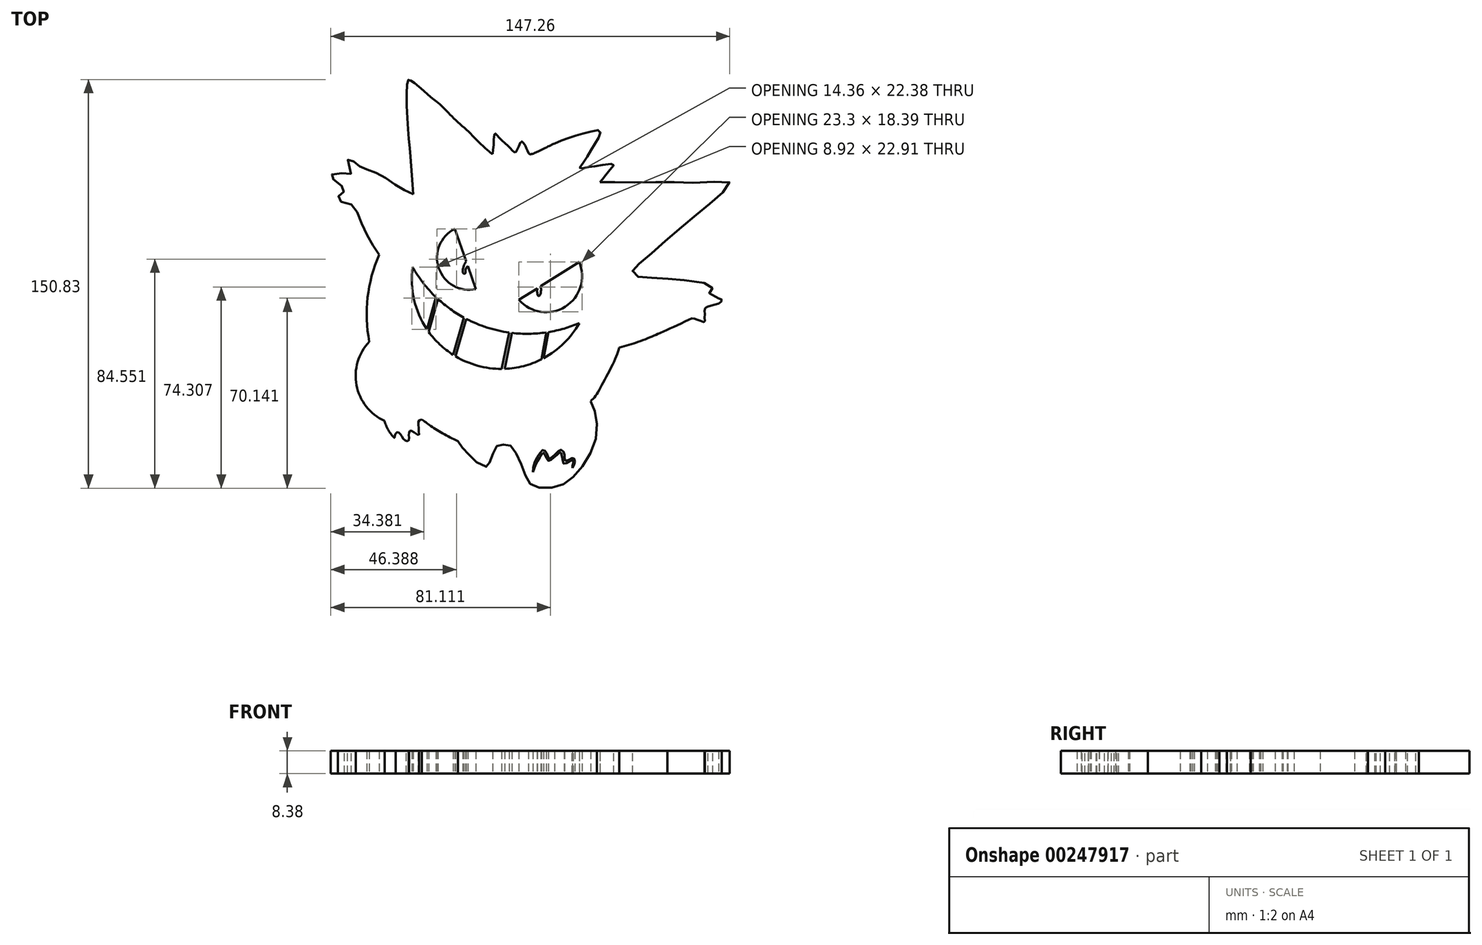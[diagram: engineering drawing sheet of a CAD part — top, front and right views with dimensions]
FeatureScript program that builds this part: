
annotation { "Feature Type Name" : "Feature", "Feature Type Description" : "" }
export const myFeature = defineFeature(function(context is Context, id is Id, definition is map)
    precondition{}
    {
        {
            var Q0;
            Q0=qCreatedBy(makeId("Top.planeOp"),FACE);
            var sketch = newSketch(context, id + "F0", { "sketchPlane" : qUnion([Q0])});
            skFitSpline(sketch, "E0", {"points": [v(-44.2, 33.5) * mm, v(-45.15, 47.05) * mm, v(-46.34, 61.31) * mm, v(-45.98, 75.74) * mm, v(-45.01, 75.48) * mm, v(-41.82, 73.05) * mm, v(-37.65, 69.34) * mm, v(-34.45, 66.9) * mm, v(-32.83, 65.28) * mm, v(-31.2, 63.6) * mm], "startDerivative": vector(-5.11, 81.73) * mm, "endDerivative": vector(23.66, -23.98) * mm});
            skFitSpline(sketch, "E1", {"points": [v(-31.2, 63.6) * mm, v(-27.62, 60.12) * mm, v(-23.5, 56.4) * mm, v(-19.52, 52.38) * mm, v(-15.7, 48.96) * mm, v(-14.85, 48.36) * mm], "startDerivative": vector(15.94, -15.97) * mm, "endDerivative": vector(7.05, -4.53) * mm});
            skFitSpline(sketch, "E2", {"points": [v(-14.85, 48.36) * mm, v(-14.42, 52.34) * mm, v(-14.03, 56) * mm, v(-13.42, 55.66) * mm, v(-12.4, 54.43) * mm, v(-10.28, 52.37) * mm, v(-8.56, 50.9) * mm, v(-7.26, 49.35) * mm, v(-6.5, 48.96) * mm, v(-5.81, 49.77) * mm, v(-5.03, 51.62) * mm, v(-4.24, 53.04) * mm, v(-3.33, 52.4) * mm, v(-2.58, 50.95) * mm, v(-2.07, 49.87) * mm, v(-1.58, 48.8) * mm], "startDerivative": vector(5.39, 35.5) * mm, "endDerivative": vector(8.81, -19.6) * mm});
            skFitSpline(sketch, "E3", {"points": [v(-1.58, 48.8) * mm, v(-1.16, 48.36) * mm, v(-0.45, 48.36) * mm, v(0.8, 48.8) * mm, v(2.92, 49.77) * mm, v(5.69, 51.2) * mm, v(8.05, 52.27) * mm], "startDerivative": vector(3.64, -5.37) * mm, "endDerivative": vector(10.96, 4.83) * mm});
            skFitSpline(sketch, "E4", {"points": [v(8.05, 52.27) * mm, v(13.52, 54.43) * mm, v(19.64, 56.18) * mm, v(24.63, 57.05) * mm, v(24.76, 55.43) * mm, v(22.13, 50.95) * mm, v(19.14, 45.81) * mm, v(17.39, 43.06) * mm, v(20.01, 43.44) * mm, v(24.38, 44.06) * mm, v(29.88, 44.56) * mm, v(28.5, 42.56) * mm, v(25.88, 39.32) * mm, v(24.76, 37.94) * mm], "startDerivative": vector(58.33, 24.87) * mm, "endDerivative": vector(-20, -23.7) * mm});
            skFitSpline(sketch, "E5", {"points": [v(24.76, 37.94) * mm, v(31.5, 37.94) * mm, v(43.61, 37.94) * mm, v(53.48, 37.94) * mm, v(64.47, 37.94) * mm, v(72.59, 37.94) * mm, v(70.71, 34.7) * mm, v(64.47, 29.33) * mm, v(57.6, 23.58) * mm, v(48.23, 15.71) * mm, v(41.74, 9.84) * mm, v(37.37, 6.35) * mm, v(36.87, 4.97) * mm, v(38, 3.35) * mm, v(41.5, 2.85) * mm, v(48.98, 2.35) * mm, v(56.48, 1.73) * mm, v(65.72, 0) * mm, v(66.34, -1.15) * mm, v(64.72, -2.27) * mm, v(65.72, -3.4) * mm, v(68.6, -4.9) * mm], "startDerivative": vector(119.95, 0.13) * mm, "endDerivative": vector(83.78, -40.05) * mm});
            skFitSpline(sketch, "E6", {"points": [v(68.6, -4.9) * mm, v(69.78, -5.48) * mm, v(69.04, -6.57) * mm, v(66.63, -7.38) * mm, v(64.54, -8) * mm, v(63.57, -8.82) * mm, v(63.49, -10.53) * mm, v(63.49, -12.66) * mm, v(63.45, -13.63) * mm, v(61.86, -13.17) * mm, v(60.15, -12.58) * mm, v(58.95, -12.31) * mm, v(56.89, -13.13) * mm, v(54.13, -14.49) * mm, v(51.5, -15.65) * mm, v(49.67, -16.43) * mm], "startDerivative": vector(29.01, -7.5) * mm, "endDerivative": vector(-25.13, -10.67) * mm});
            skFitSpline(sketch, "E7", {"points": [v(49.67, -16.43) * mm, v(46.17, -18.06) * mm, v(39.55, -20.77) * mm, v(31.98, -23.14) * mm], "startDerivative": vector(-12.19, -5.79) * mm, "endDerivative": vector(-20.06, -5.79) * mm});
            skFitSpline(sketch, "E8", {"points": [v(31.98, -23.14) * mm, v(30.17, -27.89) * mm, v(25.97, -36.05) * mm, v(23.25, -40.82) * mm, v(21.32, -42.86) * mm], "startDerivative": vector(-6.07, -18.04) * mm, "endDerivative": vector(-10.87, -10.04) * mm});
            skFitSpline(sketch, "E9", {"points": [v(21.32, -42.86) * mm, v(23.25, -48.01) * mm, v(23.25, -56.68) * mm, v(19.03, -65.93) * mm, v(13.45, -72.1) * mm, v(8.08, -74.66) * mm, v(1.32, -74.56) * mm, v(-1.7, -72.48) * mm, v(-3.57, -67.9) * mm, v(-6.16, -61.98) * mm, v(-8.35, -59.17) * mm, v(-10.74, -58.86) * mm, v(-12.92, -59.17) * mm, v(-14.06, -61.04) * mm, v(-15.83, -64.89) * mm, v(-16.25, -66.97) * mm, v(-19.57, -66.13) * mm, v(-23.32, -62.8) * mm, v(-26.02, -60) * mm, v(-27.68, -57.61) * mm], "startDerivative": vector(38.6, -82.57) * mm, "endDerivative": vector(-36.05, 57.47) * mm});
            skFitSpline(sketch, "E10", {"points": [v(-27.68, -57.61) * mm, v(-34.13, -54.28) * mm, v(-38.8, -51.16) * mm, v(-40.99, -49.6) * mm], "startDerivative": vector(-16.48, 7.92) * mm, "endDerivative": vector(-8.14, 5.82) * mm});
            skFitSpline(sketch, "E11", {"points": [v(-40.99, -49.6) * mm, v(-42.15, -50.14) * mm, v(-42.21, -51.43) * mm, v(-42.08, -54.17) * mm, v(-42.05, -55.33) * mm, v(-42.99, -54.97) * mm, v(-44.18, -54.1) * mm, v(-45.2, -53.72) * mm, v(-45.6, -54.42) * mm, v(-45.76, -55.52) * mm, v(-45.72, -57.2) * mm, v(-46.24, -57.61) * mm, v(-47.4, -57.16) * mm, v(-48.4, -55.84) * mm, v(-49.14, -54.71) * mm, v(-49.91, -54.26) * mm, v(-50.68, -54.81) * mm], "startDerivative": vector(-22.74, -5.93) * mm, "endDerivative": vector(-13.81, -14.48) * mm});
            skFitSpline(sketch, "E12", {"points": [v(-50.68, -54.81) * mm, v(-50.88, -55.4) * mm, v(-50.97, -55.89) * mm, v(-51.06, -56.34) * mm, v(-51.5, -56.03) * mm, v(-52.51, -54.81) * mm, v(-53.46, -53.29) * mm, v(-54.4, -51.22) * mm, v(-54.7, -50.17) * mm], "startDerivative": vector(-2.25, -6.24) * mm, "endDerivative": vector(-1.7, 7.35) * mm});
            skArc(sketch, "E13", {"start": v(-60.36, -20.89) * mm, "mid": v(-65.08, -36.98) * mm, "end": v(-54.7, -50.17) * mm});
            skArc(sketch, "E14", {"start": v(-56.71, 11.16) * mm, "mid": v(-60.98, -4.59) * mm, "end": v(-60.36, -20.89) * mm});
            skFitSpline(sketch, "E15", {"points": [v(-56.71, 11.16) * mm, v(-60.42, 17.1) * mm, v(-64.08, 24.9) * mm, v(-66.94, 29.66) * mm, v(-71.7, 31.25) * mm, v(-71.23, 33.48) * mm, v(-69.64, 34.75) * mm, v(-71.55, 37.45) * mm, v(-74.57, 40.15) * mm, v(-71.86, 41.42) * mm, v(-67.1, 41.1) * mm, v(-67.73, 43.49) * mm, v(-68.2, 46.35) * mm, v(-65.82, 45.4) * mm, v(-63.6, 43.65) * mm, v(-59.94, 42.22) * mm, v(-54.54, 39.67) * mm, v(-48.98, 35.86) * mm, v(-44.2, 33.5) * mm], "startDerivative": vector(-51.59, 78.2) * mm, "endDerivative": vector(75.76, -32.5) * mm});
            skLineSegment(sketch, "E16", {"start": v(-21, -1.5) * mm, "end": v(-24, 7.05) * mm});
            skLineSegment(sketch, "E17", {"start": v(-5.11, -5.47) * mm, "end": v(1.66, -1.2) * mm});
            skArc(sketch, "E18", {"start": v(-28.8, 20.76) * mm, "mid": v(-34.7, 6.2) * mm, "end": v(-21, -1.5) * mm});
            skArc(sketch, "E19", {"start": v(-5.11, -5.47) * mm, "mid": v(11.98, -7.97) * mm, "end": v(17.14, 8.52) * mm});
            skArc(sketch, "E20", {"start": v(-44.37, 6.61) * mm, "mid": v(-17.56, -15.46) * mm, "end": v(17.14, -14.05) * mm});
            skArc(sketch, "E21", {"start": v(-44.37, 6.61) * mm, "mid": v(-22.18, -29.21) * mm, "end": v(17.14, -14.05) * mm});
            skFitSpline(sketch, "E22", {"points": [v(-24.6, 8.78) * mm, v(-25.5, 7.06) * mm, v(-25.84, 5.52) * mm, v(-25.74, 4.5) * mm, v(-25.17, 4.18) * mm, v(-24.84, 4.77) * mm, v(-24.83, 5.57) * mm, v(-24.61, 6.26) * mm, v(-24, 7.05) * mm], "startDerivative": vector(-5.98, -9.82) * mm, "endDerivative": vector(5.63, 6.31) * mm});
            skFitSpline(sketch, "E23", {"points": [v(1.66, -1.2) * mm, v(1.62, -2.7) * mm, v(2.03, -4) * mm, v(2.7, -3.64) * mm, v(3.02, -2.1) * mm, v(3.03, -1.25) * mm, v(2.93, -0.4) * mm], "startDerivative": vector(-0.6, -7.3) * mm, "endDerivative": vector(-0.87, 5.98) * mm});
            skLineSegment(sketch, "E24.trimOffspring", {"start": v(2.93, -0.4) * mm, "end": v(17.14, 8.52) * mm});
            skLineSegment(sketch, "E25.trimOffspring", {"start": v(-24.6, 8.78) * mm, "end": v(-28.8, 20.76) * mm});
            skLineSegment(sketch, "E26", {"start": v(-35.73, -4.47) * mm, "end": v(-39.1, -16.3) * mm});
            skLineSegment(sketch, "E27", {"start": v(-35.02, -5.14) * mm, "end": v(-38.45, -17.22) * mm});
            skLineSegment(sketch, "E28", {"start": v(-25.47, -12) * mm, "end": v(-29.44, -25.74) * mm});
            skLineSegment(sketch, "E29", {"start": v(-28.52, -26.3) * mm, "end": v(-24.54, -12.5) * mm});
            skLineSegment(sketch, "E30", {"start": v(-8.72, -17.54) * mm, "end": v(-11.48, -30.93) * mm});
            skLineSegment(sketch, "E31", {"start": v(-10.37, -30.9) * mm, "end": v(-7.7, -17.67) * mm});
            skLineSegment(sketch, "E32", {"start": v(3.16, -27.42) * mm, "end": v(4.96, -17.49) * mm});
            skLineSegment(sketch, "E33", {"start": v(4.02, -26.97) * mm, "end": v(5.76, -17.36) * mm});
            skFitSpline(sketch, "E34", {"points": [v(0, -69) * mm, v(0.47, -66.04) * mm, v(2.35, -62.44) * mm, v(3.77, -60.9) * mm, v(4.52, -61.12) * mm, v(5.21, -62.2) * mm, v(5.74, -63.73) * mm, v(6.27, -64.17) * mm, v(7.52, -63.1) * mm, v(9.43, -61.34) * mm, v(10.46, -60.81) * mm, v(11.53, -61.85) * mm, v(11.68, -63.15) * mm, v(11.77, -64.56) * mm, v(12.2, -64.89) * mm, v(14.15, -64.05) * mm, v(15.18, -63.95) * mm, v(15.5, -64.87) * mm, v(15.42, -66) * mm, v(14.6, -67.51) * mm], "startDerivative": vector(2.64, 39) * mm, "endDerivative": vector(-18.25, -27.62) * mm});
            skFitSpline(sketch, "E35", {"points": [v(0, -69) * mm, v(0.71, -67.29) * mm, v(1.52, -65.35) * mm, v(2.52, -63.6) * mm, v(3.47, -62.35) * mm, v(3.9, -61.89) * mm, v(4.33, -62.36) * mm, v(5, -63.74) * mm, v(5.56, -64.75) * mm, v(6.6, -64.66) * mm, v(7.8, -63.67) * mm, v(9.3, -62.35) * mm, v(10.2, -61.6) * mm, v(10.52, -62.04) * mm, v(10.93, -63.92) * mm, v(11.2, -65.36) * mm, v(11.59, -66.05) * mm, v(12.9, -65.38) * mm, v(14.23, -64.72) * mm, v(14.77, -64.72) * mm, v(15.01, -65.63) * mm, v(14.53, -67) * mm, v(14.6, -67.51) * mm], "startDerivative": vector(12.68, 30.22) * mm, "endDerivative": vector(5.54, -15.4) * mm});
            skSolve(sketch);
        }
        {
            var Q0;
            Q0=makeQuery(id+"F0.imprint","IMPRINT",FACE,{"disambiguationData":[TD([[makeQuery(id+"F0.imprint","IMPRINT",EDGE,{"derivedFrom":sQuery(id+"F0.wireOp",EDGE,"E0")}),-1.0]])]});
            var Q1;
            {var subQ0=sQuery(id+"F0.wireOp",EDGE,"E26");Q1=makeQuery(id+"F0.imprint","IMPRINT",FACE,{"disambiguationData":[TD([[makeQuery(id+"F0.imprint","IMPRINT",EDGE,{"derivedFrom":subQ0}),1.0]])]});}
            var Q2;
            {var subQ0=sQuery(id+"F0.wireOp",EDGE,"E28");Q2=makeQuery(id+"F0.imprint","IMPRINT",FACE,{"disambiguationData":[TD([[makeQuery(id+"F0.imprint","IMPRINT",EDGE,{"derivedFrom":subQ0}),1.0]])]});}
            var Q3;
            {var subQ0=sQuery(id+"F0.wireOp",EDGE,"E30");Q3=makeQuery(id+"F0.imprint","IMPRINT",FACE,{"disambiguationData":[TD([[makeQuery(id+"F0.imprint","IMPRINT",EDGE,{"derivedFrom":subQ0}),1.0]])]});}
            var Q4;
            {var subQ0=sQuery(id+"F0.wireOp",EDGE,"E32");Q4=makeQuery(id+"F0.imprint","IMPRINT",FACE,{"disambiguationData":[TD([[makeQuery(id+"F0.imprint","IMPRINT",EDGE,{"derivedFrom":subQ0}),-1.0]])]});}
            extrude(context, id + "F1", {"entities" : qUnion([Q0, Q1, Q2, Q3, Q4]), "depth" : 8.38 * mm});
        }
    });
